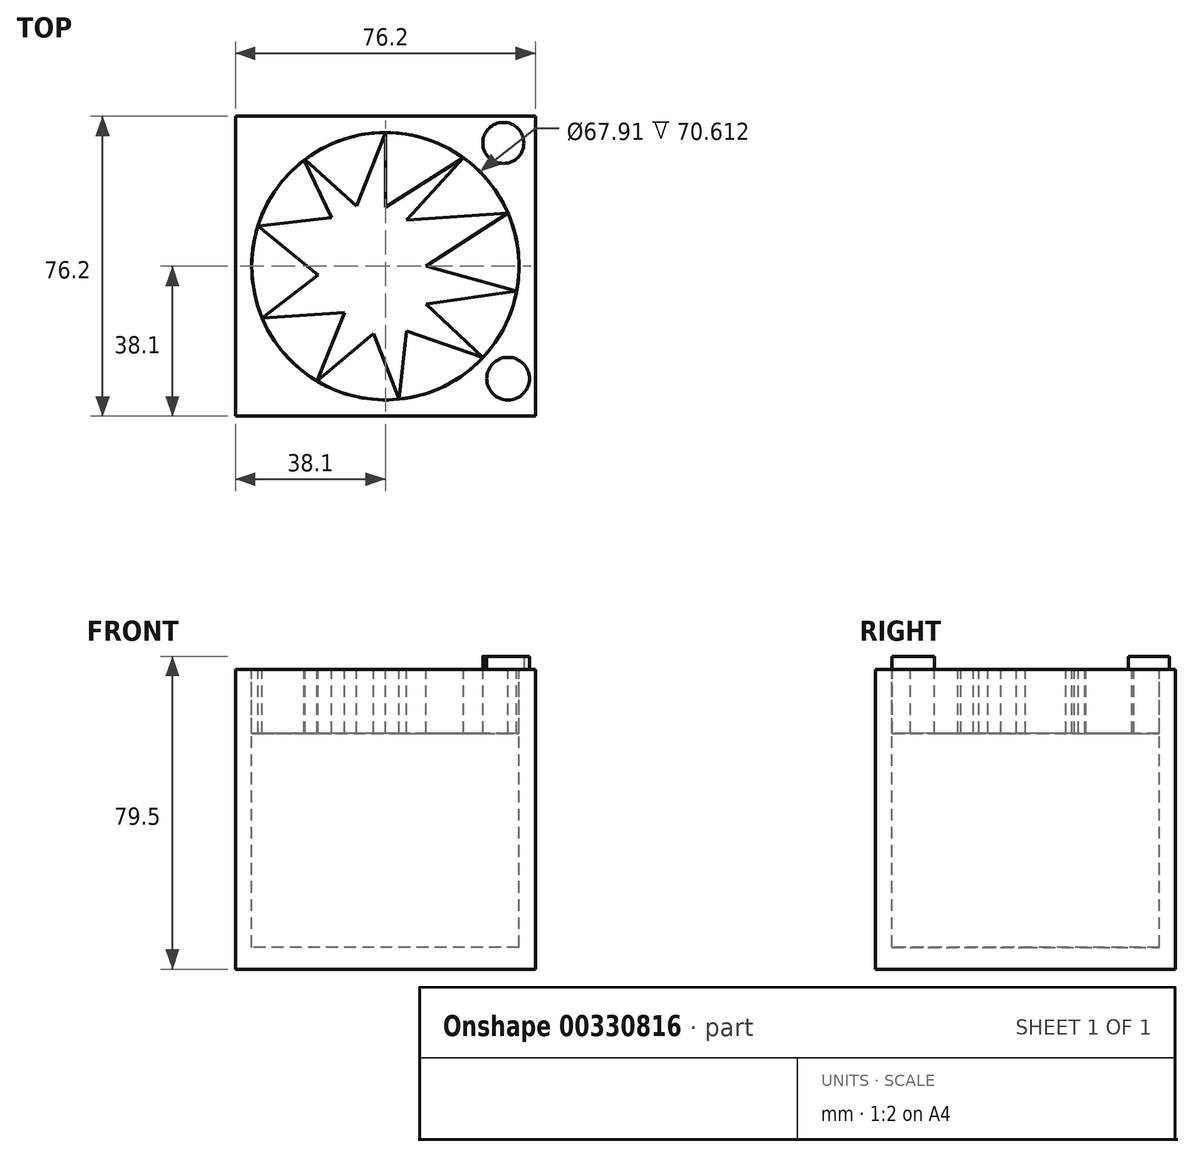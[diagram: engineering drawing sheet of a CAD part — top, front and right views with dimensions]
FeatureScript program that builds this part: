
annotation { "Feature Type Name" : "Feature", "Feature Type Description" : "" }
export const myFeature = defineFeature(function(context is Context, id is Id, definition is map)
    precondition{}
    {
        {
            var Q0;
            Q0=qCreatedBy(makeId("Top.planeOp"),FACE);
            var sketch = newSketch(context, id + "F0", { "sketchPlane" : qUnion([Q0])});
            skLineSegment(sketch, "E0.bottom", {"start": v(38.1, -38.1) * mm, "end": v(-38.1, -38.1) * mm});
            skLineSegment(sketch, "E0.top", {"start": v(38.1, 38.1) * mm, "end": v(-38.1, 38.1) * mm});
            skLineSegment(sketch, "E0.left", {"start": v(38.1, -38.1) * mm, "end": v(38.1, 38.1) * mm});
            skLineSegment(sketch, "E0.right", {"start": v(-38.1, -38.1) * mm, "end": v(-38.1, 38.1) * mm});
            skPoint(sketch, "E0.middle", {"position": v(0, 0) * mm});
            skSolve(sketch);
        }
        {
            var Q0;
            Q0 = qSketchRegion(id + "F0", true);
            extrude(context, id + "F1", {"entities" : qUnion([Q0]), "depth" : 76.2 * mm});
        }
        {
            var Q0;
            Q0=makeQuery(id+"F1.opExtrude","CAP_FACE",FACE,{"disambiguationData":[OSD([sQuery(id+"F0.wireOp",EDGE,"E0.bottom"),sQuery(id+"F0.wireOp",EDGE,"E0.top"),sQuery(id+"F0.wireOp",EDGE,"E0.left"),sQuery(id+"F0.wireOp",EDGE,"E0.right")])],"isStart":false});
            var sketch = newSketch(context, id + "F2", { "sketchPlane" : qUnion([Q0])});
            skCircle(sketch, "E1", {"center": v(0, 0) * mm, "radius": 33.95 * mm});
            skSolve(sketch);
        }
        {
            var Q0;
            Q0=makeQuery(id+"F2.imprint","IMPRINT",FACE,{"disambiguationData":[TD([[makeQuery(id+"F2.imprint","IMPRINT",EDGE,{"derivedFrom":sQuery(id+"F2.wireOp",EDGE,"E1")}),1.0]])]});
            extrude(context, id + "F3", {"entities" : qUnion([Q0]), "operationType" : NewBodyOperationType.REMOVE, "oppositeDirection" : true, "depth" : 70.61 * mm});
        }
        {
            var Q0;
            Q0=makeQuery(id+"F1.opExtrude","CAP_FACE",FACE,{"disambiguationData":[OSD([sQuery(id+"F0.wireOp",EDGE,"E0.bottom"),sQuery(id+"F0.wireOp",EDGE,"E0.top"),sQuery(id+"F0.wireOp",EDGE,"E0.left"),sQuery(id+"F0.wireOp",EDGE,"E0.right")])],"isStart":false});
            var sketch = newSketch(context, id + "F4", { "sketchPlane" : qUnion([Q0])});
            skLineSegment(sketch, "E2", {"start": v(19.8, 27.58) * mm, "end": v(5.43, 11.72) * mm});
            skLineSegment(sketch, "E3", {"start": v(5.43, 11.72) * mm, "end": v(31.18, 13.45) * mm});
            skLineSegment(sketch, "E4", {"start": v(31.18, 13.45) * mm, "end": v(10.3, 0) * mm});
            skLineSegment(sketch, "E5", {"start": v(10.3, 0) * mm, "end": v(33.36, -6.3) * mm});
            skLineSegment(sketch, "E6", {"start": v(33.36, -6.3) * mm, "end": v(10.3, -9.6) * mm});
            skLineSegment(sketch, "E7", {"start": v(10.3, -9.6) * mm, "end": v(24.86, -23.13) * mm});
            skLineSegment(sketch, "E8", {"start": v(24.86, -23.13) * mm, "end": v(5.43, -16.48) * mm});
            skLineSegment(sketch, "E9", {"start": v(5.43, -16.48) * mm, "end": v(3.46, -33.78) * mm});
            skLineSegment(sketch, "E10", {"start": v(3.46, -33.78) * mm, "end": v(-3, -17.15) * mm});
            skLineSegment(sketch, "E11", {"start": v(-3, -17.15) * mm, "end": v(-17.3, -29.21) * mm});
            skLineSegment(sketch, "E12", {"start": v(-17.3, -29.21) * mm, "end": v(-10.41, -11.82) * mm});
            skLineSegment(sketch, "E13", {"start": v(-10.41, -11.82) * mm, "end": v(-31.27, -13.22) * mm});
            skLineSegment(sketch, "E14", {"start": v(-31.27, -13.22) * mm, "end": v(-17.12, -2.3) * mm});
            skLineSegment(sketch, "E15", {"start": v(19.8, 27.58) * mm, "end": v(0, 15.05) * mm});
            skLineSegment(sketch, "E16", {"start": v(0, 15.05) * mm, "end": v(0, 33.95) * mm});
            skLineSegment(sketch, "E17", {"start": v(0, 33.95) * mm, "end": v(-7.38, 15.35) * mm});
            skLineSegment(sketch, "E18", {"start": v(-7.38, 15.35) * mm, "end": v(-20.87, 27.58) * mm});
            skLineSegment(sketch, "E19", {"start": v(-20.87, 27.58) * mm, "end": v(-13.65, 12.36) * mm});
            skLineSegment(sketch, "E20", {"start": v(-13.65, 12.36) * mm, "end": v(-32.38, 10.22) * mm});
            skLineSegment(sketch, "E21", {"start": v(-32.38, 10.22) * mm, "end": v(-17.12, -2.3) * mm});
            skSolve(sketch);
        }
        {
            var Q0;
            {var subQ0=sQuery(id+"F4.wireOp",EDGE,"E2");Q0=makeQuery(id+"F4.imprint","IMPRINT",FACE,{"disambiguationData":[TD([[makeQuery(id+"F4.imprint","IMPRINT",EDGE,{"derivedFrom":subQ0}),1.0]])]});}
            var Q1;
            {var subQ0=sQuery(id+"F4.wireOp",EDGE,"E15");Q1=makeQuery(id+"F4.imprint","IMPRINT",FACE,{"disambiguationData":[TD([[makeQuery(id+"F4.imprint","IMPRINT",EDGE,{"derivedFrom":subQ0}),-1.0]])]});}
            var Q2;
            {var subQ0=sQuery(id+"F4.wireOp",EDGE,"E17");Q2=makeQuery(id+"F4.imprint","IMPRINT",FACE,{"disambiguationData":[TD([[makeQuery(id+"F4.imprint","IMPRINT",EDGE,{"derivedFrom":subQ0}),-1.0]])]});}
            var Q3;
            {var subQ0=sQuery(id+"F4.wireOp",EDGE,"E20");Q3=makeQuery(id+"F4.imprint","IMPRINT",FACE,{"disambiguationData":[TD([[makeQuery(id+"F4.imprint","IMPRINT",EDGE,{"derivedFrom":subQ0}),-1.0]])]});}
            var Q4;
            {var subQ0=sQuery(id+"F4.wireOp",EDGE,"E14");Q4=makeQuery(id+"F4.imprint","IMPRINT",FACE,{"disambiguationData":[TD([[makeQuery(id+"F4.imprint","IMPRINT",EDGE,{"derivedFrom":subQ0}),1.0]])]});}
            var Q5;
            {var subQ0=sQuery(id+"F4.wireOp",EDGE,"E12");Q5=makeQuery(id+"F4.imprint","IMPRINT",FACE,{"disambiguationData":[TD([[makeQuery(id+"F4.imprint","IMPRINT",EDGE,{"derivedFrom":subQ0}),1.0]])]});}
            var Q6;
            {var subQ0=sQuery(id+"F4.wireOp",EDGE,"E10");Q6=makeQuery(id+"F4.imprint","IMPRINT",FACE,{"disambiguationData":[TD([[makeQuery(id+"F4.imprint","IMPRINT",EDGE,{"derivedFrom":subQ0}),1.0]])]});}
            var Q7;
            {var subQ0=sQuery(id+"F4.wireOp",EDGE,"E8");Q7=makeQuery(id+"F4.imprint","IMPRINT",FACE,{"disambiguationData":[TD([[makeQuery(id+"F4.imprint","IMPRINT",EDGE,{"derivedFrom":subQ0}),1.0]])]});}
            var Q8;
            {var subQ0=sQuery(id+"F4.wireOp",EDGE,"E6");Q8=makeQuery(id+"F4.imprint","IMPRINT",FACE,{"disambiguationData":[TD([[makeQuery(id+"F4.imprint","IMPRINT",EDGE,{"derivedFrom":subQ0}),1.0]])]});}
            var Q9;
            {var subQ0=sQuery(id+"F4.wireOp",EDGE,"E4");Q9=makeQuery(id+"F4.imprint","IMPRINT",FACE,{"disambiguationData":[TD([[makeQuery(id+"F4.imprint","IMPRINT",EDGE,{"derivedFrom":subQ0}),1.0]])]});}
            extrude(context, id + "F5", {"entities" : qUnion([Q0, Q1, Q2, Q3, Q4, Q5, Q6, Q7, Q8, Q9]), "oppositeDirection" : true, "depth" : 16.26 * mm});
        }
        {
            var Q0;
            Q0=makeQuery(id+"F1.opExtrude","CAP_FACE",FACE,{"disambiguationData":[OSD([sQuery(id+"F0.wireOp",EDGE,"E0.bottom"),sQuery(id+"F0.wireOp",EDGE,"E0.top"),sQuery(id+"F0.wireOp",EDGE,"E0.left"),sQuery(id+"F0.wireOp",EDGE,"E0.right")])],"isStart":false});
            var sketch = newSketch(context, id + "F6", { "sketchPlane" : qUnion([Q0])});
            skCircle(sketch, "E22", {"center": v(29.97, 31.34) * mm, "radius": 5.21 * mm});
            skCircle(sketch, "E23", {"center": v(31.17, -28.55) * mm, "radius": 5.42 * mm});
            skSolve(sketch);
        }
        {
            var Q0;
            Q0=makeQuery(id+"F6.imprint","IMPRINT",FACE,{"disambiguationData":[TD([[makeQuery(id+"F6.imprint","IMPRINT",EDGE,{"derivedFrom":sQuery(id+"F6.wireOp",EDGE,"E23")}),1.0]])]});
            var Q1;
            Q1=makeQuery(id+"F6.imprint","IMPRINT",FACE,{"disambiguationData":[TD([[makeQuery(id+"F6.imprint","IMPRINT",EDGE,{"derivedFrom":sQuery(id+"F6.wireOp",EDGE,"E22")}),1.0]])]});
            extrude(context, id + "F7", {"entities" : qUnion([Q0, Q1]), "operationType" : NewBodyOperationType.ADD, "depth" : 3.3 * mm});
        }
    });
